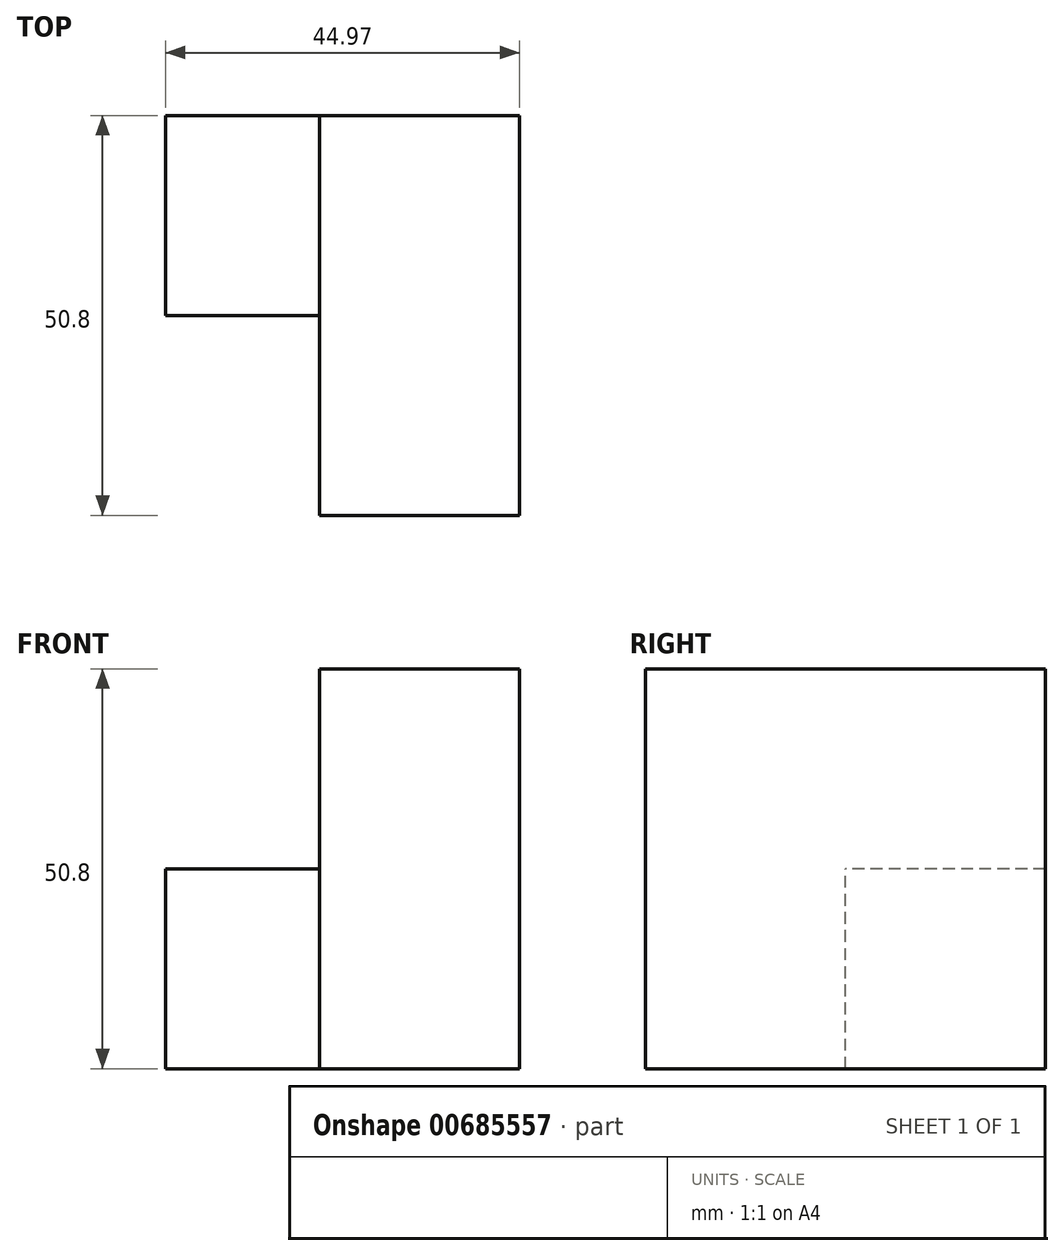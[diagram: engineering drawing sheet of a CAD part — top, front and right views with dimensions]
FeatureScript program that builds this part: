
annotation { "Feature Type Name" : "Feature", "Feature Type Description" : "" }
export const myFeature = defineFeature(function(context is Context, id is Id, definition is map)
    precondition{}
    {
        {
            var Q0;
            Q0=qCreatedBy(makeId("Front.planeOp"),FACE);
            var sketch = newSketch(context, id + "F0", { "sketchPlane" : qUnion([Q0])});
            skLineSegment(sketch, "E0", {"start": v(0, 0) * mm, "end": v(0, 50.8) * mm});
            skLineSegment(sketch, "E1", {"start": v(0, 50.8) * mm, "end": v(-25.4, 50.8) * mm});
            skLineSegment(sketch, "E2", {"start": v(-25.4, 50.8) * mm, "end": v(-25.4, 0) * mm});
            skLineSegment(sketch, "E3", {"start": v(-25.4, 0) * mm, "end": v(0, 0) * mm});
            skSolve(sketch);
        }
        {
            var Q0;
            Q0=qCreatedBy(makeId("Front.planeOp"),FACE);
            var sketch = newSketch(context, id + "F1", { "sketchPlane" : qUnion([Q0])});
            skLineSegment(sketch, "E4", {"start": v(-19.57, 0) * mm, "end": v(-19.57, 25.4) * mm});
            skLineSegment(sketch, "E5", {"start": v(-19.57, 25.4) * mm, "end": v(-44.97, 25.4) * mm});
            skLineSegment(sketch, "E6", {"start": v(-44.97, 25.4) * mm, "end": v(-44.97, 0) * mm});
            skLineSegment(sketch, "E7", {"start": v(-44.97, 0) * mm, "end": v(-19.57, 0) * mm});
            skSolve(sketch);
        }
        {
            var Q0;
            Q0 = qSketchRegion(id + "F1", true);
            extrude(context, id + "F2", {"entities" : qUnion([Q0]), "depth" : 25.4 * mm, "offsetDistance" : 25.4 * mm});
        }
        {
            var Q0;
            Q0=makeQuery(id+"F0.imprint","IMPRINT",FACE,{"disambiguationData":[TD([[makeQuery(id+"F0.imprint","IMPRINT",EDGE,{"derivedFrom":sQuery(id+"F0.wireOp",EDGE,"E0")}),1.0]])]});
            extrude(context, id + "F3", {"entities" : qUnion([Q0]), "operationType" : NewBodyOperationType.ADD, "depth" : 50.8 * mm, "offsetDistance" : 25.4 * mm});
        }
    });
